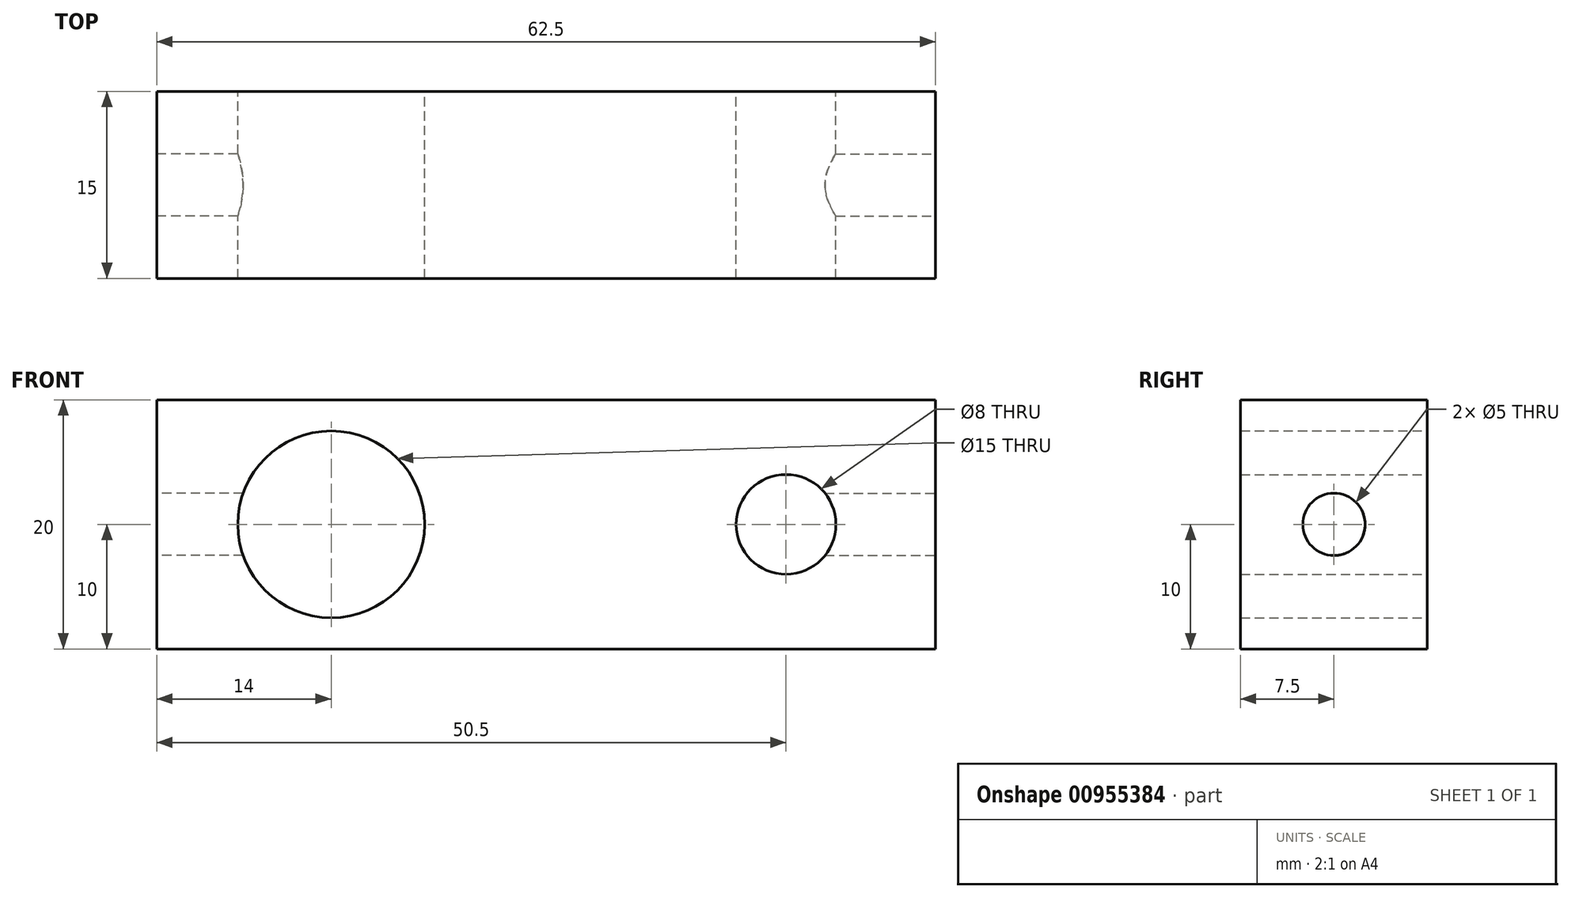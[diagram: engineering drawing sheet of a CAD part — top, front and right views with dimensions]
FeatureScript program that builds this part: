
annotation { "Feature Type Name" : "Feature", "Feature Type Description" : "" }
export const myFeature = defineFeature(function(context is Context, id is Id, definition is map)
    precondition{}
    {
        {
            var Q0;
            Q0=qCreatedBy(makeId("Front.planeOp"),FACE);
            var sketch = newSketch(context, id + "F0", { "sketchPlane" : qUnion([Q0])});
            skLineSegment(sketch, "E0.bottom", {"start": v(29.25, 10) * mm, "end": v(-33.25, 10) * mm});
            skLineSegment(sketch, "E0.top", {"start": v(29.25, -10) * mm, "end": v(-33.25, -10) * mm});
            skLineSegment(sketch, "E0.left", {"start": v(29.25, 10) * mm, "end": v(29.25, -10) * mm});
            skLineSegment(sketch, "E0.right", {"start": v(-33.25, 10) * mm, "end": v(-33.25, -10) * mm});
            skCircle(sketch, "E1", {"center": v(17.25, 0) * mm, "radius": 4 * mm});
            skCircle(sketch, "E2", {"center": v(-19.25, 0) * mm, "radius": 7.5 * mm});
            skSolve(sketch);
        }
        {
            var Q0;
            Q0=makeQuery(id+"F0.imprint","IMPRINT",FACE,{"disambiguationData":[TD([[makeQuery(id+"F0.imprint","IMPRINT",EDGE,{"derivedFrom":sQuery(id+"F0.wireOp",EDGE,"E0.bottom")}),1.0]])]});
            extrude(context, id + "F1", {"entities" : qUnion([Q0]), "depth" : 7.5 * mm, "offsetDistance" : 25 * mm});
        }
        {
            var Q0;
            Q0=makeQuery(id+"F1.opExtrude","CAP_FACE",FACE,{"disambiguationData":[OSD([sQuery(id+"F0.wireOp",EDGE,"E0.bottom"),sQuery(id+"F0.wireOp",EDGE,"E0.top"),sQuery(id+"F0.wireOp",EDGE,"E0.left"),sQuery(id+"F0.wireOp",EDGE,"E0.right"),sQuery(id+"F0.wireOp",EDGE,"E1")])],"isStart":false});
            extrude(context, id + "F2", {"entities" : qUnion([Q0]), "operationType" : NewBodyOperationType.ADD, "depth" : 7.5 * mm, "offsetDistance" : 25 * mm});
        }
        {
            var Q0;
            {var subQ0=sQuery(id+"F0.wireOp",EDGE,"E0.right");Q0=makeQuery(id+"F2.boolean.opBoolean","MERGE",FACE,{"derivedFrom":[makeQuery(id+"F1.opExtrude","SWEPT_FACE",FACE,{"disambiguationData":[OSD([subQ0])]}),makeQuery(id+"F2.opExtrude","SWEPT_FACE",FACE,{"disambiguationData":[OSD([subQ0])]})]});}
            var sketch = newSketch(context, id + "F3", { "sketchPlane" : qUnion([Q0])});
            skCircle(sketch, "E3", {"center": v(7.5, 0) * mm, "radius": 2.5 * mm});
            skSolve(sketch);
        }
        {
            var Q0;
            Q0 = qSketchRegion(id + "F3", true);
            extrude(context, id + "F4", {"entities" : qUnion([Q0]), "operationType" : NewBodyOperationType.REMOVE, "oppositeDirection" : true, "depth" : 10 * mm, "offsetDistance" : 25 * mm});
        }
        {
            var Q0;
            {var subQ0=sQuery(id+"F0.wireOp",EDGE,"E0.left");Q0=makeQuery(id+"F2.boolean.opBoolean","MERGE",FACE,{"derivedFrom":[makeQuery(id+"F1.opExtrude","SWEPT_FACE",FACE,{"disambiguationData":[OSD([subQ0])]}),makeQuery(id+"F2.opExtrude","SWEPT_FACE",FACE,{"disambiguationData":[OSD([subQ0])]})]});}
            var sketch = newSketch(context, id + "F5", { "sketchPlane" : qUnion([Q0])});
            skCircle(sketch, "E4", {"center": v(-7.5, 0) * mm, "radius": 2.5 * mm});
            skSolve(sketch);
        }
        {
            var Q0;
            Q0 = qSketchRegion(id + "F5", true);
            extrude(context, id + "F6", {"entities" : qUnion([Q0]), "operationType" : NewBodyOperationType.REMOVE, "oppositeDirection" : true, "depth" : 12 * mm, "offsetDistance" : 25 * mm});
        }
    });
